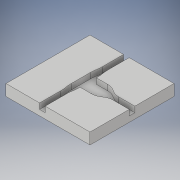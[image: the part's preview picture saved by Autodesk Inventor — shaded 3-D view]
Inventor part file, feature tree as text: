
AUTODESK INVENTOR PART (.ipt)
format: ipt  version: 2019 (Build 230136000, 136)  size: 173,056 bytes
history: native  units: mm
features: extrude x2, sketch x2
ambient origin geometry x8: Origin, YZ Plane, XZ Plane, XY Plane, X Axis, Y Axis, Z Axis, Center Point
bodies: Solid1 (feature_tree)
feature tree (4):
  extrude  "Extrusion1"  Depth=150.0mm
  extrude  "Extrusion2"  Depth=10.0mm
  sketch  "Sketch1"  dims[d0=150.0mm d1=150.0mm]
  sketch  "Sketch2"  dims[d18=34.0mm d19=13.5mm d20=2.5mm d21=20.0mm d22=29.0mm d23=20.0mm d24=2.5mm d25=58.25mm d26=58.0mm d27=10.0mm d28=70.0mm d29=58.25mm d30=10.0mm d31=1.75mm d32=0.0mm d33=10.0mm d34=1.75mm d35=30.0mm d36=15.0mm d37=106.75mm d38=121.75mm d39=10.0mm d40=44.0mm d41=10.0mm d42=10.0mm d43=10.0mm d44=0.0mm d45=10.0mm d46=0.0mm]
